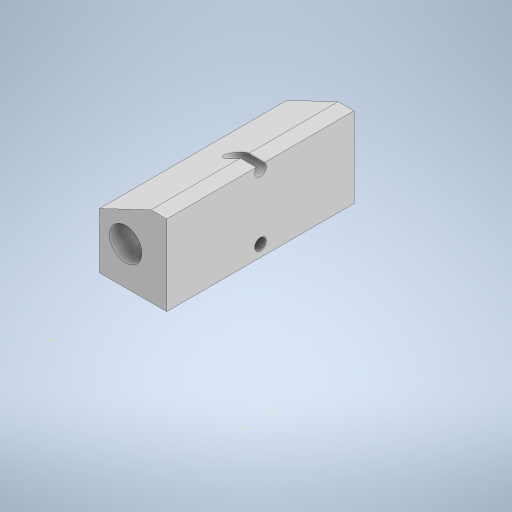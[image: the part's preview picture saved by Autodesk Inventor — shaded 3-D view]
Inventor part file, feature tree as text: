
AUTODESK INVENTOR PART (.ipt)
format: ipt  version: 2024 (Build 280153020, 153B)  size: 577,536 bytes
history: native  units: mm
features: sketch x32, extrude x27, move_body x4, chamfer x3, plane x3, split x3, boolean_combine x2, other x1, fillet x1, imported_body x1
ambient origin geometry x8: Origin, YZ Plane, XZ Plane, XY Plane, X Axis, Y Axis, Z Axis, Center Point
bodies: Solid1 (feature_tree), Solid2 (feature_tree), Solid3 (feature_tree), Solid4 (feature_tree), Solid5 (feature_tree), Solid6 (feature_tree), Solid7 (feature_tree), Solid8 (feature_tree)
feature tree (77):
  other  "Repaired Geometry1"
  extrude  "Extrusion1"  Depth=16.0mm
  sketch  "Sketch2"  dims[d2=15.0mm d3=0.0mm d4=10.0mm]
  extrude  "Extrusion2"  Depth=10.0mm
  chamfer  "Chamfer1"  Distance=21.25mm
  extrude  "Extrusion3"  Depth=10.0mm TaperAngle=0.0deg
  extrude  "Extrusion4"  Depth=11.5mm TaperAngle=0.0deg
  extrude  "Extrusion5"  Depth=1.0mm TaperAngle=0.0deg
  chamfer  "Chamfer2"  Distance=6.0mm Angle=45.0deg
  sketch  "Sketch6"  dims[d14=7.0mm d15=11.5mm d16=0.0mm]
  extrude  "Extrusion6"  Depth=9.0mm
  extrude  "Extrusion7"  Depth=11.5mm TaperAngle=0.0deg
  chamfer  "Chamfer3"  Distance=11.5mm Angle=45.0deg
  sketch  "Sketch9"  dims[d26=3.3mm d27=45.25mm d28=0.0mm d29=11.5mm d30=5.5mm d31=45.0deg]
  extrude  "Extrusion8"  Depth=65.75mm TaperAngle=0.0deg
  extrude  "Extrusion9"  Depth=9.0mm TaperAngle=0.0deg
  extrude  "Extrusion10"  Depth=13.0mm TaperAngle=0.0deg
  sketch  "Sketch13"  dims[d43=24.0mm d44=21.0mm d45=0.0mm]
  extrude  "Extrusion11"  Depth=24.0mm TaperAngle=0.0deg
  extrude  "Extrusion12"  TaperAngle=0.0deg  [1 undecoded]
  extrude  "Extrusion13"  Depth=6.0mm TaperAngle=0.0deg
  plane  "Work Plane1"
  split  "Split1"
  move_body  "Move Body1"
  extrude  "Extrusion14"  Depth=0.5mm TaperAngle=0.0deg
  move_body  "Move Body2"
  fillet  "Fillet1"  Radius=10.0mm
  extrude  "Extrusion15"  Depth=10.0mm TaperAngle=0.0deg
  sketch  "Sketch19"  dims[d71=29.5mm d72=0.0mm d73=13.75mm]
  sketch  "Sketch20"  dims[d74=26.0mm d75=0.0mm d76=-5.0mm d77=0.0mm d78=0.0mm]
  extrude  "Extrusion16"  Depth=1.0mm
  extrude  "Extrusion18"  Depth=13.75mm
  extrude  "Extrusion19"  TaperAngle=0.0deg  [1 undecoded]
  sketch  "Sketch23"  dims[d86=11.5mm d87=0.0mm d88=11.5mm d89=0.0mm]
  sketch  "Sketch24"  dims[d90=4.5mm d91=38.0mm d92=0.0mm]
  extrude  "Extrusion20"  TaperAngle=0.0deg  [1 undecoded]
  plane  "Work Plane2"
  boolean_combine  "Combine1"
  split  "Split2"
  extrude  "Extrusion21"  Depth=11.5mm TaperAngle=0.0deg
  move_body  "Move Body3"
  boolean_combine  "Combine2"
  plane  "Work Plane3"
  split  "Split3"
  move_body  "Move Body4"
  extrude  "Extrusion23"  Depth=38.0mm TaperAngle=0.0deg
  extrude  "Extrusion24"  Depth=41.0mm TaperAngle=0.0deg
  extrude  "Extrusion25"  Depth=32.0mm TaperAngle=0.0deg
  extrude  "Extrusion26"  Depth=32.0mm TaperAngle=0.0deg
  extrude  "Extrusion28"  [1 undecoded]
  extrude  "Extrusion29"  [1 undecoded]
  extrude  "Extrusion30"  [1 undecoded]
  sketch  "Sketch1"  dims[d0=36.0mm d1=16.0mm]
  sketch  "Sketch3"  dims[d5=10.0mm]
  sketch  "Sketch4"  dims[d6=3.3mm d7=21.25mm d8=0.0mm]
  sketch  "Sketch5"  dims[d9=10.0mm d10=5.5mm d11=45.0deg d12=10.0mm d13=0.0mm]
  sketch  "Sketch7"  dims[d17=3.3mm d18=1.0mm d19=0.0mm d20=6.0mm d21=11.5mm d22=45.0deg]
  sketch  "Sketch8"  dims[d23=15.0mm d24=0.0mm d25=9.0mm]
  sketch  "Sketch10"  dims[d32=2.0mm d33=65.75mm d34=0.0mm]
  sketch  "Sketch11"  dims[d35=0.5mm d36=0.0mm d37=9.0mm d38=0.0mm]
  sketch  "Sketch12"  dims[d39=0.5mm d40=0.0mm d41=13.0mm d42=0.0mm]
  sketch  "Sketch14"  dims[d46=12.25mm d47=-12.0mm d48=0.0mm d49=0.0mm]
  sketch  "Sketch15"  dims[d50=30.0mm d51=0.0mm d52=6.0mm d53=0.0mm d54=0.0mm d55=4.0mm]
  sketch  "Sketch16"  dims[d56=0.5mm d57=0.0mm d58=0.5mm d59=0.0mm d64=10.0mm d65=0.0mm]
  sketch  "Sketch17"  dims[d66=3.0mm d67=10.0mm d68=0.0mm]
  sketch  "Sketch18"  dims[d69=1.0mm d70=31.0mm]
  sketch  "Sketch22"  dims[d79=0.0mm d80=0.0mm d81=0.0mm d82=-30.0mm]
  sketch  "Sketch25"  dims[d93=5.1mm d94=41.0mm d95=0.0mm]
  sketch  "Sketch26"  dims[d98=5.5mm d99=32.0mm d100=0.0mm]
  imported_body  "Base1"
  sketch  "Sketch28"  dims[d101=32.0mm d102=0.0mm d103=32.0mm d104=0.0mm]
  sketch  "Sketch29"
  sketch  "Sketch30"
  sketch  "Sketch31"
  sketch  "Sketch33"
  sketch  "Sketch34"
  sketch  "Sketch35"
note: 6 required parameter values undecoded (feature->parameter linkage not recoverable at this tier; creation-order binding heuristic only, values carry confidence <= 0.55)
